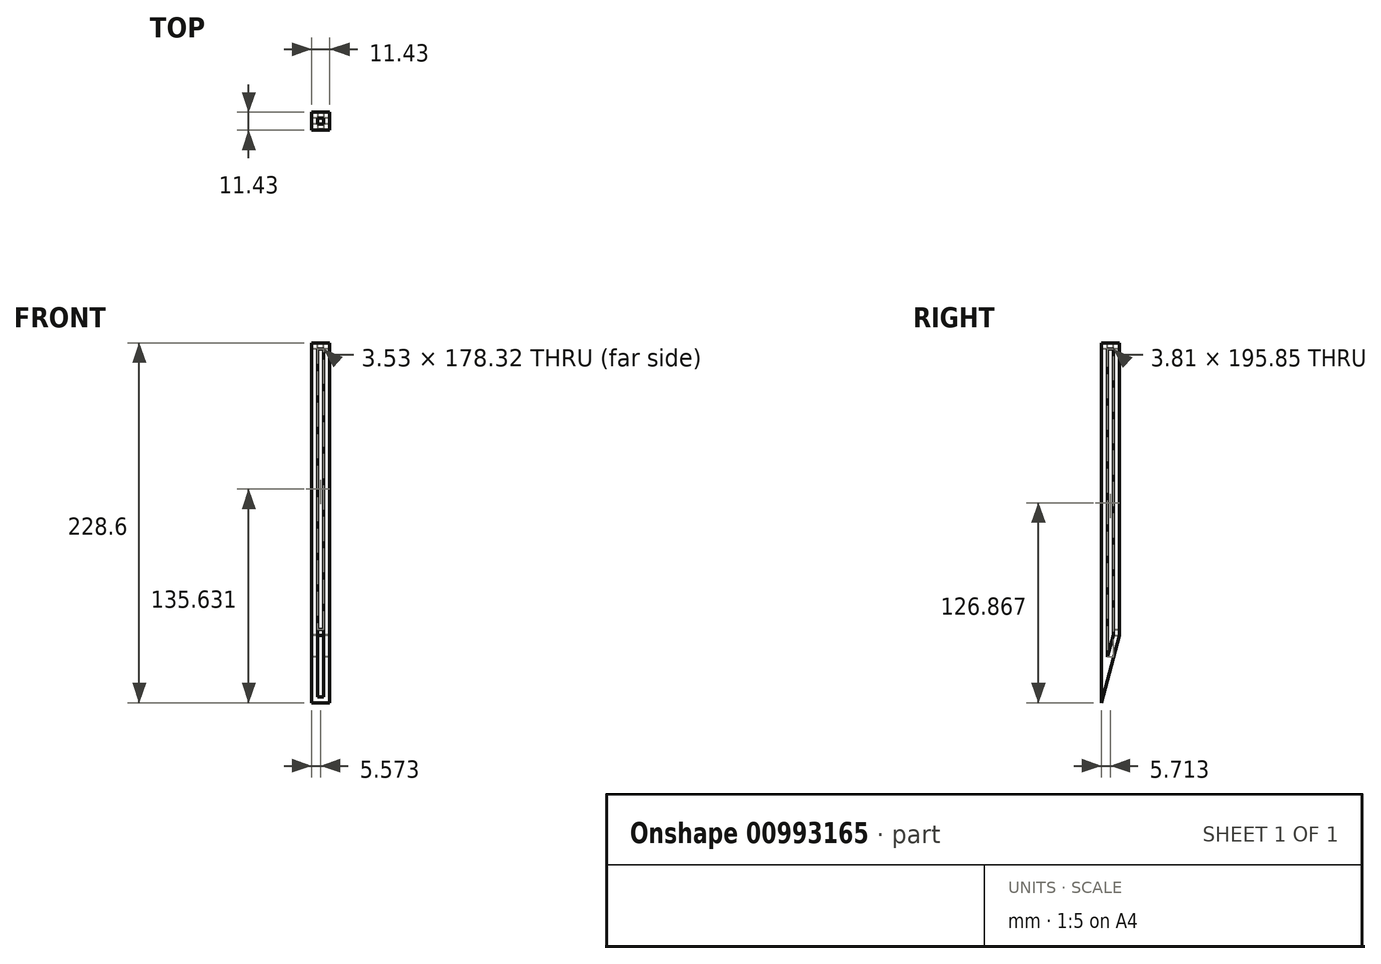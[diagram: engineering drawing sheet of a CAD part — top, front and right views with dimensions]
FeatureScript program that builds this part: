
annotation { "Feature Type Name" : "Feature", "Feature Type Description" : "" }
export const myFeature = defineFeature(function(context is Context, id is Id, definition is map)
    precondition{}
    {
        {
            var Q0;
            Q0=qCreatedBy(makeId("Right.planeOp"),FACE);
            var sketch = newSketch(context, id + "F0", { "sketchPlane" : qUnion([Q0])});
            skLineSegment(sketch, "E0.bottom", {"start": v(-43.88, 1.87) * mm, "end": v(-32.45, 1.87) * mm});
            skLineSegment(sketch, "E0.left", {"start": v(-43.88, 1.87) * mm, "end": v(-43.88, -226.73) * mm});
            skLineSegment(sketch, "E1.bottom", {"start": v(-40.07, 1.87) * mm, "end": v(-36.26, 1.87) * mm});
            skLineSegment(sketch, "E2", {"start": v(-43.88, -1.94) * mm, "end": v(-32.45, -1.94) * mm});
            skLineSegment(sketch, "E3", {"start": v(-43.88, -226.73) * mm, "end": v(-32.45, -184.07) * mm});
            skLineSegment(sketch, "E4", {"start": v(-43.88, -212) * mm, "end": v(-32.45, -169.35) * mm});
            skLineSegment(sketch, "E5", {"start": v(-40.07, -212.5) * mm, "end": v(-40.07, 1.87) * mm});
            skLineSegment(sketch, "E6", {"start": v(-32.45, 1.87) * mm, "end": v(-32.45, -184.07) * mm});
            skLineSegment(sketch, "E7", {"start": v(-36.26, 1.87) * mm, "end": v(-36.26, -198.29) * mm});
            skSolve(sketch);
        }
        {
            var Q0;
            Q0 = qSketchRegion(id + "F0", true);
            extrude(context, id + "F1", {"entities" : qUnion([Q0]), "depth" : 11.43 * mm, "offsetDistance" : 25.4 * mm});
        }
        {
            var Q0;
            Q0=makeQuery(id+"F1.opExtrude","SWEPT_FACE",FACE,{"disambiguationData":[OSD([sQuery(id+"F0.wireOp",EDGE,"E0.left")])]});
            var sketch = newSketch(context, id + "F2", { "sketchPlane" : qUnion([Q0])});
            skLineSegment(sketch, "E8.bottom", {"start": v(3.8, -1.94) * mm, "end": v(7.34, -1.94) * mm});
            skLineSegment(sketch, "E8.top", {"start": v(3.81, -222.92) * mm, "end": v(7.34, -222.92) * mm});
            skLineSegment(sketch, "E8.left", {"start": v(3.8, -1.94) * mm, "end": v(3.81, -222.92) * mm});
            skLineSegment(sketch, "E8.right", {"start": v(7.34, -1.94) * mm, "end": v(7.34, -222.92) * mm});
            skSolve(sketch);
        }
        {
            var Q0;
            Q0=makeQuery(id+"F2.imprint","IMPRINT",FACE,{"disambiguationData":[TD([[makeQuery(id+"F2.imprint","IMPRINT",EDGE,{"derivedFrom":sQuery(id+"F2.wireOp",EDGE,"E8.bottom")}),-1.0]])]});
            extrude(context, id + "F3", {"entities" : qUnion([Q0]), "operationType" : NewBodyOperationType.REMOVE, "oppositeDirection" : true, "depth" : 25.4 * mm, "offsetDistance" : 25.4 * mm});
        }
        {
            var Q0;
            Q0=makeQuery(id+"F1.opExtrude","SWEPT_FACE",FACE,{"disambiguationData":[OSD([sQuery(id+"F0.wireOp",EDGE,"E6")])]});
            var sketch = newSketch(context, id + "F4", { "sketchPlane" : qUnion([Q0])});
            skLineSegment(sketch, "E9.bottom", {"start": v(-11.43, -184.07) * mm, "end": v(0, -184.07) * mm});
            skLineSegment(sketch, "E9.top", {"start": v(-11.43, -180.26) * mm, "end": v(0, -180.26) * mm});
            skLineSegment(sketch, "E9.left", {"start": v(-11.43, -184.07) * mm, "end": v(-11.43, -180.26) * mm});
            skLineSegment(sketch, "E9.right", {"start": v(0, -184.07) * mm, "end": v(0, -180.26) * mm});
            skSolve(sketch);
        }
        {
            var Q0;
            {var subQ0=sQuery(id+"F4.wireOp",EDGE,"E9.bottom");var subQ1=makeQuery(id+"F1.opExtrude","SWEPT_FACE",FACE,{"disambiguationData":[OSD([sQuery(id+"F0.wireOp",EDGE,"E6")])]});var subQ2=makeQuery(id+"F3.boolean.opBoolean","INTERSECT",EDGE,{"derivedFrom":[subQ1,makeQuery(id+"F3.opExtrude","SWEPT_FACE",FACE,{"disambiguationData":[OSD([sQuery(id+"F2.wireOp",EDGE,"E8.left")])]})]});var subQ3=makeQuery(id+"F4.imprint","INTERSECT",VERTEX,{"derivedFrom":[subQ2,subQ0]});Q0=makeQuery(id+"F4.imprint","IMPRINT",FACE,{"disambiguationData":[TD([[makeQuery(id+"F4.imprint","IMPRINT",EDGE,{"disambiguationData":[TD([[subQ3,1.0]])],"derivedFrom":subQ0}),1.0]])]});}
            extrude(context, id + "F5", {"entities" : qUnion([Q0]), "operationType" : NewBodyOperationType.ADD, "oppositeDirection" : true, "depth" : 3.8 * mm, "offsetDistance" : 25.4 * mm});
        }
        {
            var Q0;
            Q0=makeQuery(id+"F1.opExtrude","SWEPT_FACE",FACE,{"disambiguationData":[OSD([sQuery(id+"F0.wireOp",EDGE,"E0.bottom"),sQuery(id+"F0.wireOp",EDGE,"E1.bottom")])]});
            var sketch = newSketch(context, id + "F6", { "sketchPlane" : qUnion([Q0])});
            skLineSegment(sketch, "E10.bottom", {"start": v(7.62, -36.26) * mm, "end": v(3.81, -36.26) * mm});
            skLineSegment(sketch, "E10.top", {"start": v(7.62, -40.07) * mm, "end": v(3.81, -40.07) * mm});
            skLineSegment(sketch, "E10.left", {"start": v(7.62, -36.26) * mm, "end": v(7.62, -40.07) * mm});
            skLineSegment(sketch, "E10.right", {"start": v(3.81, -36.26) * mm, "end": v(3.81, -40.07) * mm});
            skPoint(sketch, "E10.middle", {"position": v(5.72, -38.17) * mm});
            skPoint(sketch, "E10.middle.positionSnap0", {"position": v(5.72, -32.45) * mm});
            skPoint(sketch, "E10.centerSnap0", {"position": v(5.72, -32.45) * mm});
            skSolve(sketch);
        }
        {
            var Q0;
            Q0=makeQuery(id+"F6.imprint","IMPRINT",FACE,{"disambiguationData":[TD([[makeQuery(id+"F6.imprint","IMPRINT",EDGE,{"derivedFrom":sQuery(id+"F6.wireOp",EDGE,"E10.bottom")}),1.0]])]});
            extrude(context, id + "F7", {"entities" : qUnion([Q0]), "operationType" : NewBodyOperationType.REMOVE, "oppositeDirection" : true, "depth" : 25.4 * mm, "offsetDistance" : 25.4 * mm});
        }
    });
